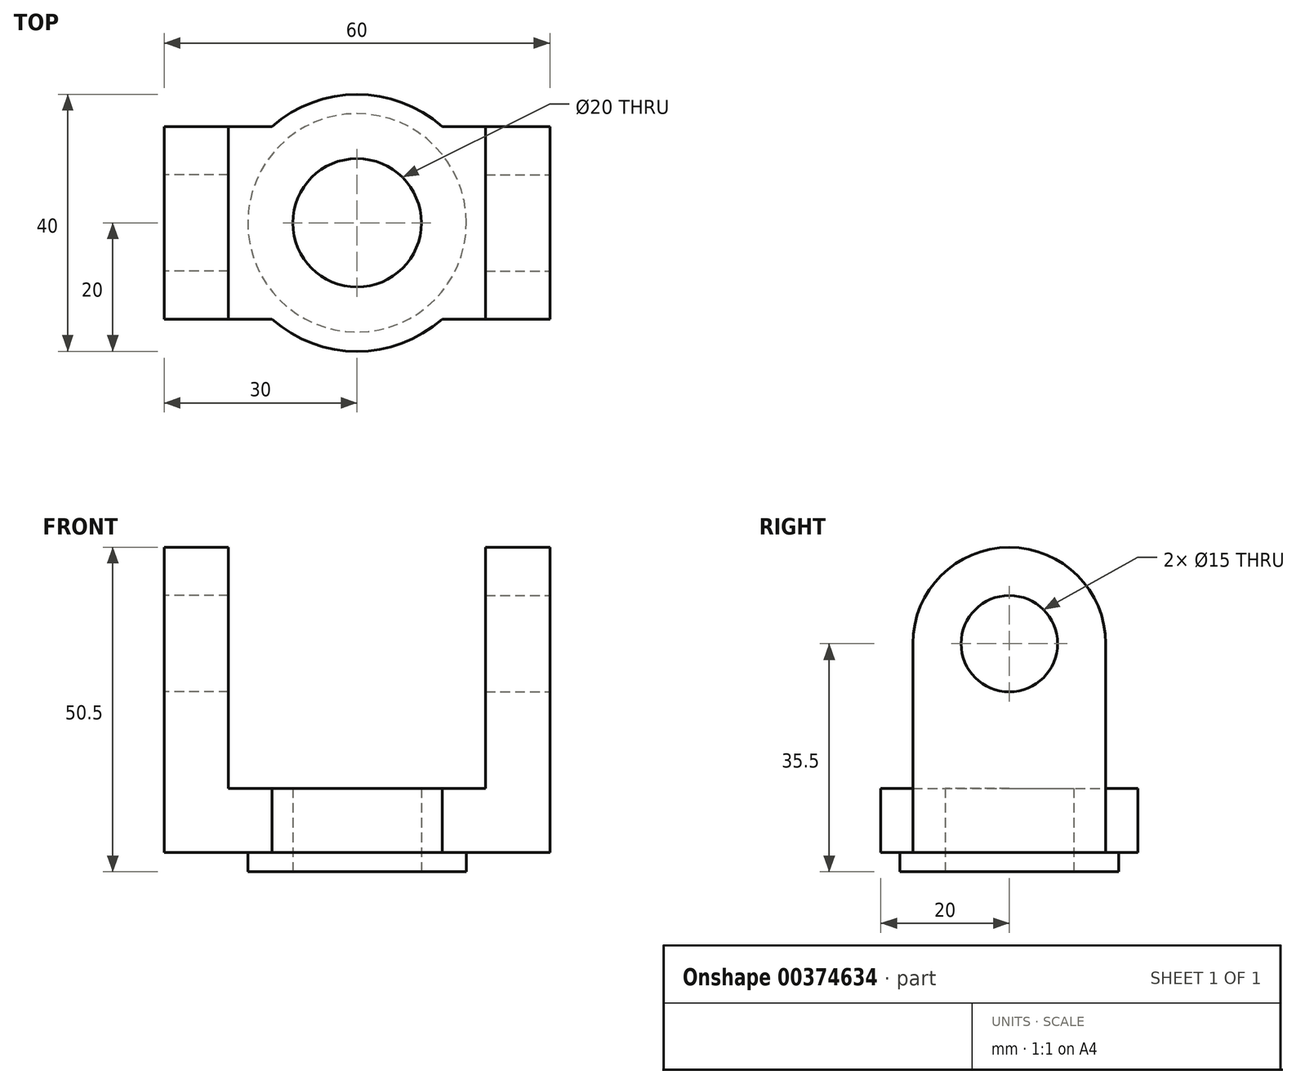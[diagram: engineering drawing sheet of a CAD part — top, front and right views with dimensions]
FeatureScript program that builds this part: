
annotation { "Feature Type Name" : "Feature", "Feature Type Description" : "" }
export const myFeature = defineFeature(function(context is Context, id is Id, definition is map)
    precondition{}
    {
        {
            var Q0;
            Q0=qCreatedBy(makeId("Top.planeOp"),FACE);
            var sketch = newSketch(context, id + "F0", { "sketchPlane" : qUnion([Q0])});
            skArc(sketch, "E0", {"start": v(-13.23, -15) * mm, "mid": v(0, -20) * mm, "end": v(13.23, -15) * mm});
            skLineSegment(sketch, "E1.bottom", {"start": v(-30, -15) * mm, "end": v(-13.23, -15) * mm});
            skLineSegment(sketch, "E1.top", {"start": v(-30, 15) * mm, "end": v(-13.23, 15) * mm});
            skLineSegment(sketch, "E1.left", {"start": v(-30, -15) * mm, "end": v(-30, 15) * mm});
            skLineSegment(sketch, "E1.right", {"start": v(30, -15) * mm, "end": v(30, 15) * mm});
            skLineSegment(sketch, "E2.trimOffspring", {"start": v(13.23, -15) * mm, "end": v(30, -15) * mm});
            skArc(sketch, "E3.trimOffspring", {"start": v(13.23, 15) * mm, "mid": v(0, 20) * mm, "end": v(-13.23, 15) * mm});
            skLineSegment(sketch, "E4.trimOffspring", {"start": v(13.23, 15) * mm, "end": v(30, 15) * mm});
            skCircle(sketch, "E5", {"center": v(0, 0) * mm, "radius": 10 * mm});
            skSolve(sketch);
        }
        {
            var Q0;
            Q0 = qSketchRegion(id + "F0", true);
            extrude(context, id + "F1", {"entities" : qUnion([Q0]), "depth" : 10 * mm});
        }
        {
            var Q0;
            Q0=makeQuery(id+"F1.opExtrude","SWEPT_FACE",FACE,{"disambiguationData":[OSD([sQuery(id+"F0.wireOp",EDGE,"E1.right")])]});
            var sketch = newSketch(context, id + "F2", { "sketchPlane" : qUnion([Q0])});
            skLineSegment(sketch, "E6", {"start": v(-15, 10) * mm, "end": v(-15, 32.5) * mm});
            skLineSegment(sketch, "E7", {"start": v(-15, 32.5) * mm, "end": v(15, 32.5) * mm, "construction": true});
            skLineSegment(sketch, "E8", {"start": v(15, 32.5) * mm, "end": v(15, 10) * mm});
            skLineSegment(sketch, "E9", {"start": v(15, 10) * mm, "end": v(-15, 10) * mm});
            skArc(sketch, "E10", {"start": v(15, 32.5) * mm, "mid": v(0, 47.5) * mm, "end": v(-15, 32.5) * mm});
            skCircle(sketch, "E11", {"center": v(0, 32.5) * mm, "radius": 7.5 * mm});
            skSolve(sketch);
        }
        {
            var Q0;
            Q0 = qSketchRegion(id + "F2", true);
            extrude(context, id + "F3", {"entities" : qUnion([Q0]), "operationType" : NewBodyOperationType.ADD, "oppositeDirection" : true, "depth" : 10 * mm});
        }
        {
            var Q0;
            Q0=makeQuery(id+"F1.opExtrude","SWEPT_BODY",BODY,{"disambiguationData":[OSD([sQuery(id+"F0.wireOp",EDGE,"E0"),sQuery(id+"F0.wireOp",EDGE,"E1.bottom"),sQuery(id+"F0.wireOp",EDGE,"E1.top"),sQuery(id+"F0.wireOp",EDGE,"E1.left"),sQuery(id+"F0.wireOp",EDGE,"E1.right"),sQuery(id+"F0.wireOp",EDGE,"E2.trimOffspring"),sQuery(id+"F0.wireOp",EDGE,"E3.trimOffspring"),sQuery(id+"F0.wireOp",EDGE,"E4.trimOffspring"),sQuery(id+"F0.wireOp",EDGE,"E5")])]});
            var Q1;
            Q1=qCreatedBy(makeId("Right.planeOp"),FACE);
            mirror(context, id + "F4", {"operationType" : NewBodyOperationType.ADD, "entities" : qUnion([Q0]), "mirrorPlane" : qUnion([Q1])});
        }
        {
            var Q0;
            Q0=makeQuery(id+"F1.opExtrude","CAP_FACE",FACE,{"disambiguationData":[OSD([sQuery(id+"F0.wireOp",EDGE,"E0"),sQuery(id+"F0.wireOp",EDGE,"E1.bottom"),sQuery(id+"F0.wireOp",EDGE,"E1.top"),sQuery(id+"F0.wireOp",EDGE,"E1.left"),sQuery(id+"F0.wireOp",EDGE,"E1.right"),sQuery(id+"F0.wireOp",EDGE,"E2.trimOffspring"),sQuery(id+"F0.wireOp",EDGE,"E3.trimOffspring"),sQuery(id+"F0.wireOp",EDGE,"E4.trimOffspring"),sQuery(id+"F0.wireOp",EDGE,"E5")])],"isStart":true});
            var sketch = newSketch(context, id + "F5", { "sketchPlane" : qUnion([Q0])});
            skCircle(sketch, "E12", {"center": v(0, 0) * mm, "radius": 17 * mm});
            skSolve(sketch);
        }
        {
            var Q0;
            Q0 = qSketchRegion(id + "F5", true);
            extrude(context, id + "F6", {"entities" : qUnion([Q0]), "operationType" : NewBodyOperationType.ADD, "depth" : 3 * mm});
        }
        {
            var Q0;
            Q0=makeQuery(id+"F6.opExtrude","CAP_FACE",FACE,{"disambiguationData":[OSD([sQuery(id+"F5.wireOp",EDGE,"E12")])],"isStart":false});
            var sketch = newSketch(context, id + "F7", { "sketchPlane" : qUnion([Q0])});
            skCircle(sketch, "E13", {"center": v(0, 0) * mm, "radius": 10 * mm});
            skSolve(sketch);
        }
        {
            var Q0;
            Q0 = qSketchRegion(id + "F7", true);
            extrude(context, id + "F8", {"entities" : qUnion([Q0]), "operationType" : NewBodyOperationType.REMOVE, "endBound" : BoundingType.THROUGH_ALL, "oppositeDirection" : true, "depth" : 25 * mm});
        }
    });
